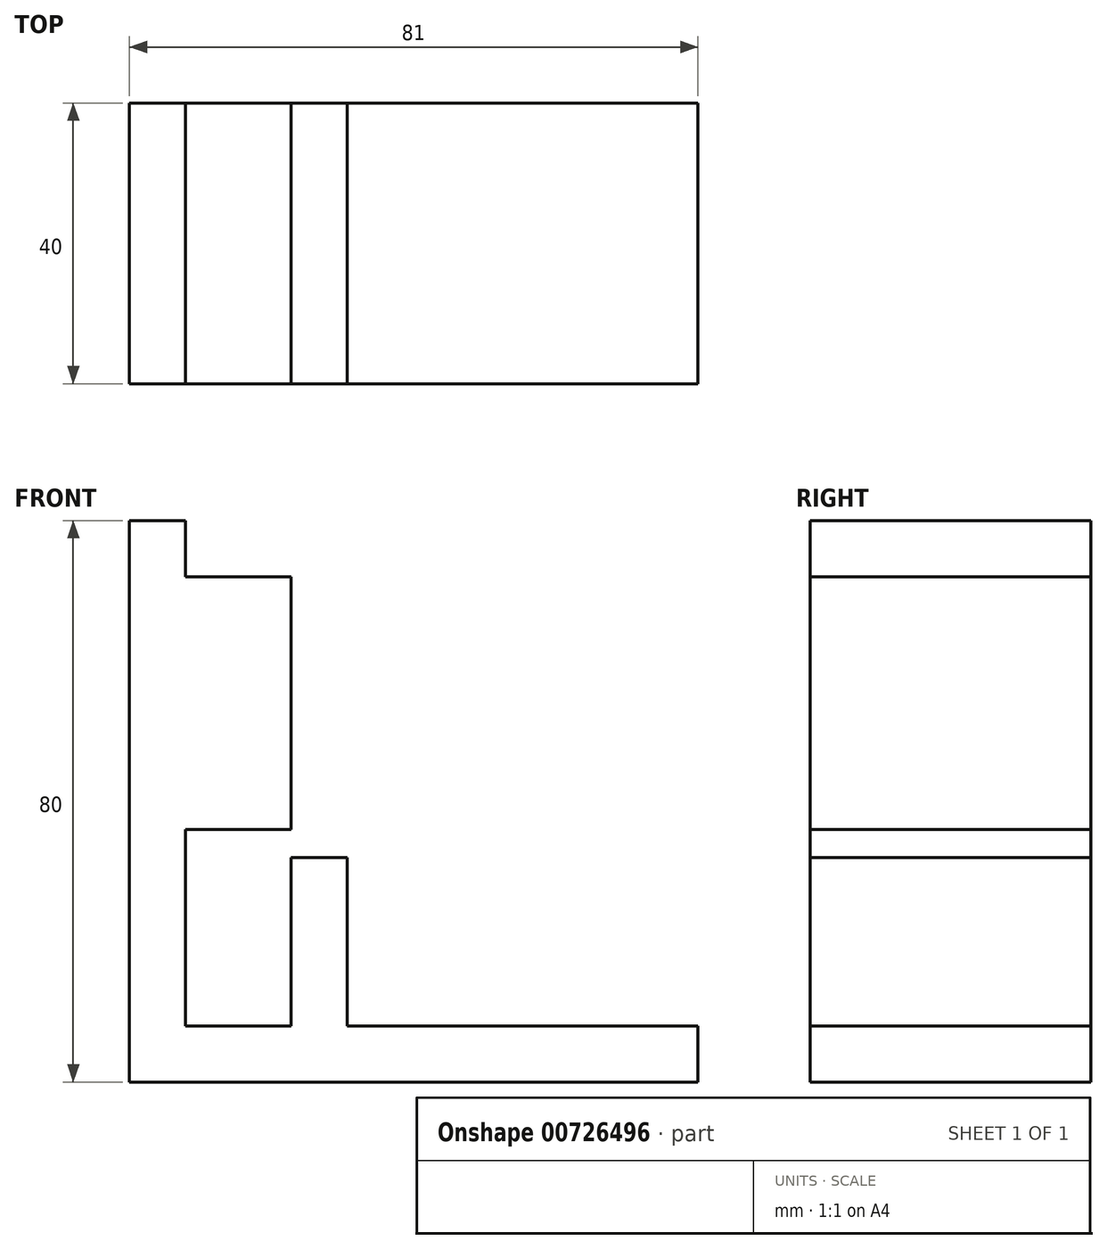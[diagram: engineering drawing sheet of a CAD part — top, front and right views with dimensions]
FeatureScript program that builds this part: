
annotation { "Feature Type Name" : "Feature", "Feature Type Description" : "" }
export const myFeature = defineFeature(function(context is Context, id is Id, definition is map)
    precondition{}
    {
        {
            var Q0;
            Q0=qCreatedBy(makeId("Front.planeOp"),FACE);
            var sketch = newSketch(context, id + "F0", { "sketchPlane" : qUnion([Q0])});
            skLineSegment(sketch, "E0", {"start": v(0, 0) * mm, "end": v(0, 80) * mm});
            skLineSegment(sketch, "E1", {"start": v(0, 80) * mm, "end": v(8, 80) * mm});
            skLineSegment(sketch, "E2", {"start": v(8, 80) * mm, "end": v(8, 8) * mm});
            skLineSegment(sketch, "E3", {"start": v(8, 8) * mm, "end": v(23, 8) * mm});
            skLineSegment(sketch, "E4", {"start": v(23, 8) * mm, "end": v(23, 32) * mm});
            skLineSegment(sketch, "E5", {"start": v(23, 32) * mm, "end": v(31, 32) * mm});
            skLineSegment(sketch, "E6", {"start": v(31, 32) * mm, "end": v(31, 8) * mm});
            skLineSegment(sketch, "E7", {"start": v(31, 8) * mm, "end": v(56, 8) * mm});
            skLineSegment(sketch, "E8", {"start": v(56, 8) * mm, "end": v(81, 8) * mm});
            skLineSegment(sketch, "E9", {"start": v(81, 8) * mm, "end": v(81, 0) * mm});
            skLineSegment(sketch, "E10", {"start": v(81, 0) * mm, "end": v(0, 0) * mm});
            skLineSegment(sketch, "E11", {"start": v(8, 8) * mm, "end": v(8, 39.82) * mm});
            skLineSegment(sketch, "E12", {"start": v(8, 36) * mm, "end": v(23, 36) * mm});
            skLineSegment(sketch, "E13", {"start": v(23, 36) * mm, "end": v(23, 72) * mm});
            skLineSegment(sketch, "E14", {"start": v(23, 72) * mm, "end": v(8, 72) * mm});
            skSolve(sketch);
        }
        {
            var Q0;
            {var subQ0=sQuery(id+"F0.wireOp",EDGE,"E12");Q0=makeQuery(id+"F0.imprint","IMPRINT",FACE,{"disambiguationData":[TD([[makeQuery(id+"F0.imprint","IMPRINT",EDGE,{"derivedFrom":subQ0}),1.0]])]});}
            var Q1;
            Q1 = qSketchRegion(id + "FwTlWKi0H16s8Yl_0", true);
            var Q2;
            Q2 = qSketchRegion(id + "FBdeD0wpAn6DXoD_0", true);
            var Q3;
            Q3 = qSketchRegion(id + "F0", true);
            extrude(context, id + "F1", {"entities" : qUnion([Q0, Q1, Q2, Q3]), "oppositeDirection" : true, "depth" : 40 * mm, "offsetDistance" : 25 * mm});
        }
    });
